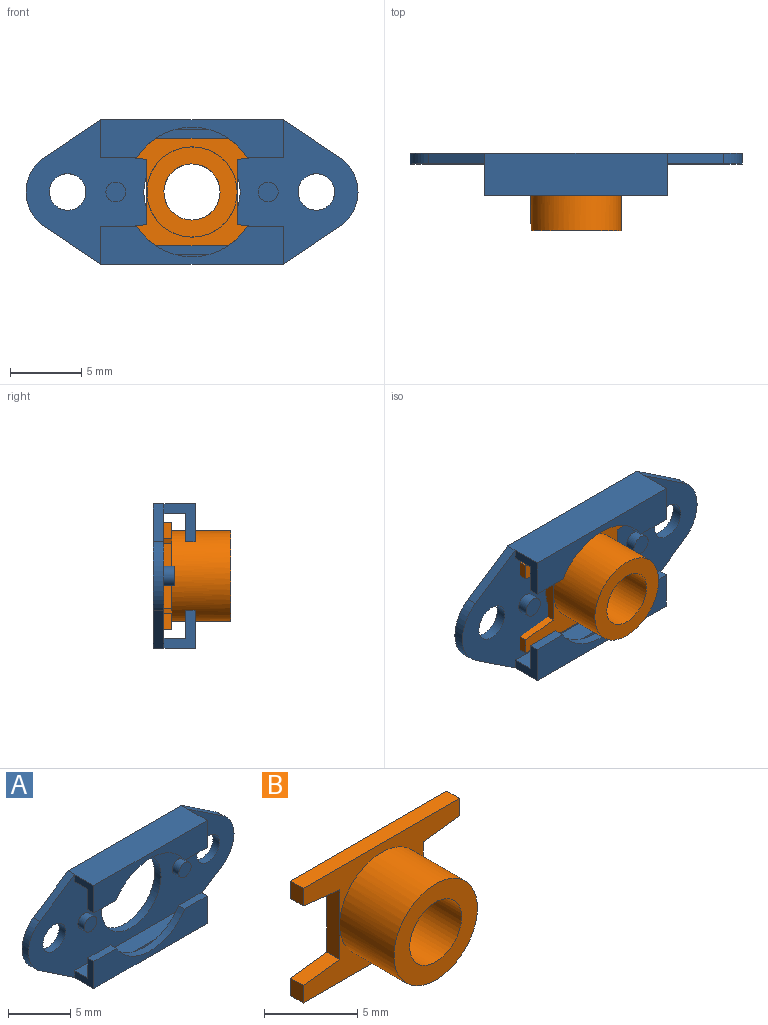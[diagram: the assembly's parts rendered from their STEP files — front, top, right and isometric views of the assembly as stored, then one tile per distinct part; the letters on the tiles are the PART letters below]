
ASSEMBLY  parts=2 mates=1
PART A: 37 faces, bbox 23.3x2.9x10.1 mm
  f0: plane 2.54x0.69mm, normal (0,0,1), area 1.7mm2, adj f2,f8,f27,f36
  f1: plane 5.15x1.98mm, normal (0,1,0), area 7mm2, adj f5,f6,f32,f36
  f2: plane 5.15x1.98mm, normal (0,1,0), area 7mm2, adj f0,f8,f32,f36
  f3: plane 2.54x0.69mm, normal (0,0,-1), area 1.7mm2, adj f4,f28,f29,f33
  f4: plane 5.15x1.98mm, normal (0,1,0), area 7mm2, adj f3,f28,f31,f33
  f5: plane 2.54x0.69mm, normal (0,0,1), area 1.7mm2, adj f1,f6,f27,f36
  f6: plane 2.67x2.18mm, normal (-1,0,0), area 2.9mm2, adj f1,f5,f11,f12,f27,f32
  f7: cylinder r=3.38mm len=6.76mm, axis (0,-1,0), area 15.6mm2, adj f11,f13
  f8: plane 2.67x2.18mm, normal (1,0,0), area 2.9mm2, adj f0,f2,f11,f12,f27,f32
  f9: plane 2.67x2.18mm, normal (-1,0,0), area 2.9mm2, adj f10,f11,f14,f29,f30,f31
  f10: plane 2.54x0.69mm, normal (0,0,-1), area 1.7mm2, adj f9,f29,f30,f33
  f11: plane 23.29x10.11mm, normal (0,-1,0), area 130.6mm2, adj f6,f7,f8,f9,f15,f16,f17,f18
  f12: plane 12.83x2.92mm, normal (0,0,-1), area 37.5mm2, adj f6,f8,f13,f17,f19,f27
  f13: plane 23.29x10.11mm, normal (0,1,0), area 151.2mm2, adj f7,f12,f14,f15,f16,f17,f18,f19
  f14: plane 12.83x2.92mm, normal (0,0,1), area 37.5mm2, adj f9,f13,f15,f20,f28,f29
  f15: plane 3.93x2.63mm, normal (0.56,0,0.83), area 3.5mm2, adj f11,f13,f14,f16
  f16: cylinder r=2.92mm len=4.86mm, axis (0,-1,0), area 4.2mm2, adj f11,f13,f15,f19
  f17: plane 3.93x2.63mm, normal (-0.56,0,-0.83), area 3.5mm2, adj f11,f12,f13,f18
  f18: cylinder r=2.92mm len=4.86mm, axis (0,-1,0), area 4.2mm2, adj f11,f13,f17,f20
  f19: plane 3.93x2.63mm, normal (0.56,0,-0.83), area 3.5mm2, adj f11,f12,f13,f16
  f20: plane 3.93x2.63mm, normal (-0.56,0,0.83), area 3.5mm2, adj f11,f13,f14,f18
  f21: cylinder r=1.28mm len=2.57mm, axis (0,-1,0), area 5.9mm2, adj f11,f13
  f22: cylinder r=1.28mm len=2.57mm, axis (0,-1,0), area 5.9mm2, adj f11,f13
  f23: cylinder r=0.7mm len=1.4mm, axis (0,1,0), area 3.2mm2, adj f11,f24
  f24: plane 1.4x1.4mm, normal (0,-1,0), area 1.5mm2, adj f23
  f25: cylinder r=0.7mm len=1.4mm, axis (0,1,0), area 3.2mm2, adj f11,f26
  f26: plane 1.4x1.4mm, normal (0,-1,0), area 1.5mm2, adj f25
  f27: plane 12.83x2.67mm, normal (0,-1,0), area 22.4mm2, adj f0,f5,f6,f8,f12,f36
  f28: plane 2.67x2.18mm, normal (1,0,0), area 2.9mm2, adj f3,f4,f11,f14,f29,f31
  f29: plane 12.83x2.67mm, normal (0,-1,0), area 22.4mm2, adj f3,f9,f10,f14,f28,f33
  f30: plane 5.15x1.98mm, normal (0,1,0), area 7mm2, adj f9,f10,f31,f33
  f31: plane 12.83x1.5mm, normal (0,0,-1), area 19.2mm2, adj f4,f9,f11,f28,f30,f34
  f32: plane 12.83x1.5mm, normal (0,0,1), area 19.2mm2, adj f1,f2,f6,f8,f11,f35
  f33: cylinder r=4.55mm len=7.74mm, axis (0,-1,0), area 6.3mm2, adj f3,f4,f10,f29,f30,f34
  f34: plane 2.52x0.18mm, normal (0,-1,0), area 0.3mm2, adj f31,f33
  f35: plane 2.52x0.18mm, normal (0,-1,0), area 0.3mm2, adj f32,f36
  f36: cylinder r=4.55mm len=7.74mm, axis (0,-1,0), area 6.3mm2, adj f0,f1,f2,f5,f27,f35
PART B: 18 faces, bbox 11.8x5.1x7.5 mm
  f0: plane 1.14x0.97mm, normal (1,0,0), area 1.1mm2, adj f2,f4,f6,f13
  f1: plane 1.14x0.97mm, normal (-1,0,0), area 1.1mm2, adj f2,f4,f6,f17
  f2: plane 11.84x3.76mm, normal (0,-1,0), area 15.3mm2, adj f0,f1,f6,f9,f13,f14,f16,f17
  f3: plane 11.84x3.76mm, normal (0,-1,0), area 15.3mm2, adj f5,f7,f8,f9,f12,f14,f15,f16
  f4: plane 11.84x7.52mm, normal (0,1,0), area 49.8mm2, adj f0,f1,f5,f6,f7,f8,f11,f12
  f5: plane 1.14x0.97mm, normal (1,0,0), area 1.1mm2, adj f3,f4,f8,f12
  f6: plane 11.84x0.97mm, normal (0,0,1), area 11.4mm2, adj f0,f1,f2,f4
  f7: plane 1.14x0.97mm, normal (-1,0,0), area 1.1mm2, adj f3,f4,f8,f15
  f8: plane 11.84x0.97mm, normal (0,0,-1), area 11.4mm2, adj f3,f4,f5,f7
  f9: cylinder r=3.16mm len=6.32mm, axis (0,1,0), area 81.8mm2, adj f2,f3,f10
  f10: plane 6.32x6.32mm, normal (0,-1,0), area 19.2mm2, adj f9,f11
  f11: cylinder r=1.97mm len=5.08mm, axis (0,-1,0), area 62.8mm2, adj f4,f10
  f12: plane 2.76x0.97mm, normal (0.12,0,0.99), area 2.7mm2, adj f3,f4,f5,f14
  f13: plane 2.76x0.97mm, normal (0.12,0,-0.99), area 2.7mm2, adj f0,f2,f4,f14
  f14: plane 4.57x0.97mm, normal (1,0,0), area 4.4mm2, adj f2,f3,f4,f12,f13
  f15: plane 2.76x0.97mm, normal (-0.12,0,0.99), area 2.7mm2, adj f3,f4,f7,f16
  f16: plane 4.57x0.97mm, normal (-1,0,0), area 4.4mm2, adj f2,f3,f4,f15,f17
  f17: plane 2.76x0.97mm, normal (-0.12,0,-0.99), area 2.7mm2, adj f1,f2,f4,f16
PLACE A t=(-7.41,0,1.36)mm
PLACE B t=(-7.41,-0.32,1.36)mm
MATE slider B.f9 <-> A.f7  axis (0,1,0) through (-7.41,-0.32,1.36)mm
